# Revit family: AV1080001_Grifería para Lavamanos 8 pulgadas Aluvia Triceta
name_source: partatom
category: Plumbing Fixtures
units: mm (PartAtom-declared; Revit-internal decimal feet)

## family parameters
Cut with Voids When Loaded = No
Host = Face
OmniClass Number = 23.31.00.00
Part Type = Normal
Room Calculation Point = No
Round Connector Dimension = Use Diameter
Shared = No

## types (1)
- AV1080001_Grifería para Lavamanos 8 pulgadas Aluvia Triceta
    Alto = 132 mm  [stored 0.433071 ft]
    Ancho = 260 mm  [stored 0.853018 ft]
    Capacidad de flujo = 60 psi : 5,7 L/min.
    Creado por = BIMBAU
    Default Elevation = 1219 mm
    Description = Aluvia integra líneas y formas como las de una erosión aluvial, su forma robusta está inspirada en el agua esculpiendo las rocas a través de los años dando paso a superficies más suaves, amigables y limpias evitando que haya acumulación de impurezas. El conjunto de manijas es el resultado de su diseño ergonómico, brindando un agarre cómodo sin importar el agua y el jabón • Grifería ultra ahorro, consumo de 5,7 litros por minuto.
• Cierre fácil giro práctico de tan sólo 90º.
• Acabado superior, mayor espesor en el cromado que lo hace más brillante y
resistente a la corrosión.
• Mayor ángulo de salida permite mayor alcance y más comodidad en el
momento del uso.
• Fácil limpieza: Diseño que evita la acumulación de impurezas.
    Fecha de creación = 10/03/2021
    Garantía = 30 Años
    Garantía Acabados = 2 Años
    Manufacturer = Corona
    Material = Corona_Aluminio
    Model = Grifería lavamanos 8 pulgadas triceta
    Peso neto = 310 gr. - 0,68 lb.
    Presion maxima = 125 psi (862 Kpa).
    Presion minima = 20 psi (138 Kpa)
    Profundidad = 150 mm
    Temperatura de uso = 5ºC a 71ºC.
    URL = https://bimbau.s3.amazonaws.com
    Vida útil = 500.000 ciclos.

note: [stored X ft] marks values corroborated as IEEE doubles in the binary element streams (Revit-internal decimal feet)

## geometry (parser evidence)
native form markers: Sweep x6
no freeform markers — native parametric forms only
